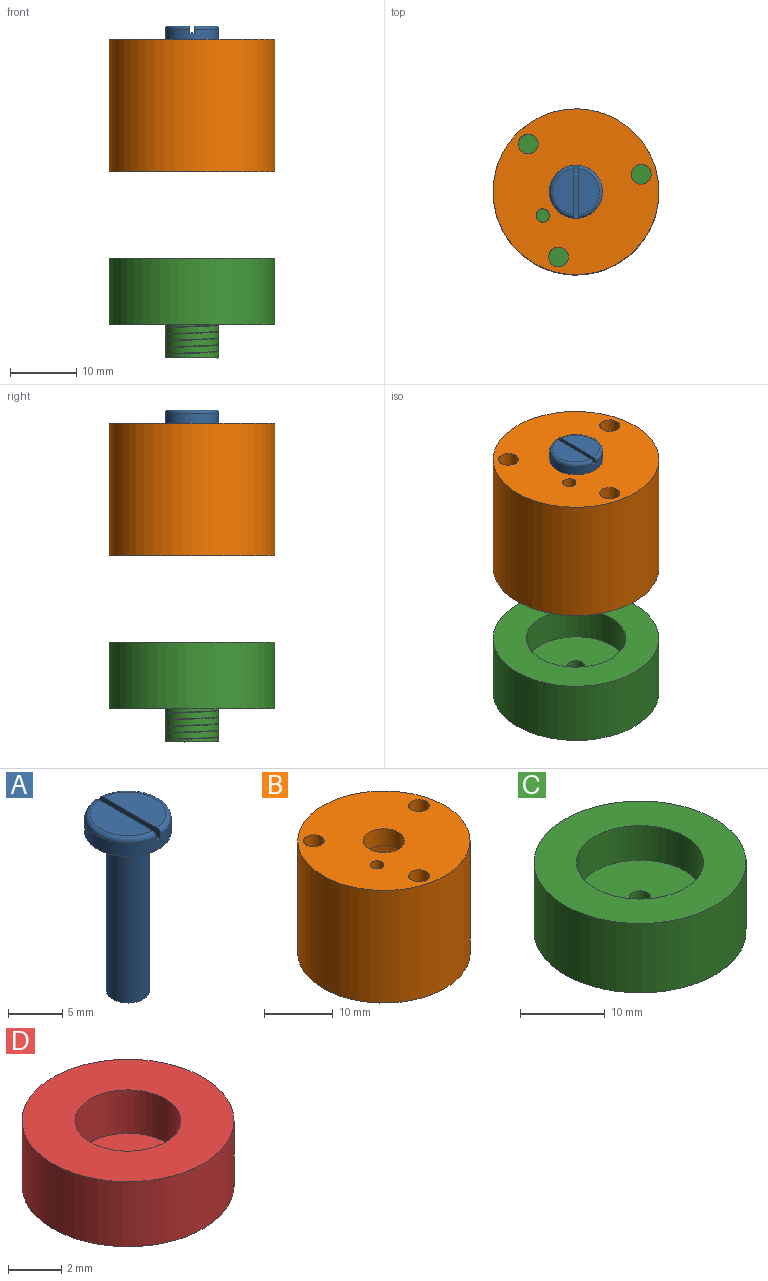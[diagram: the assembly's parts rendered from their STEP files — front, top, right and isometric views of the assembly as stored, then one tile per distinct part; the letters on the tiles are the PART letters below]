
ASSEMBLY  parts=4 mates=4
PART A: 11 faces, bbox 8.7x8.7x20 mm
  f0: plane 6.97x3.19mm, normal (0,0,1), area 17.1mm2, adj f7,f9
  f1: torus R=3.5mm, axis (0,0,-1), area 8.9mm2, adj f5,f6,f10
  f2: plane 8x8mm, normal (0,0,-1), area 37.7mm2, adj f3,f6
  f3: cylinder r=2mm len=18mm, axis (0,0,1), area 226.2mm2, adj f2,f4
  f4: plane 4x4mm, normal (0,0,-1), area 12.6mm2, adj f3
  f5: plane 6.97x3.2mm, normal (0,0,1), area 17.1mm2, adj f1,f10
  f6: cylinder r=4mm len=8mm, axis (0,0,1), area 37.1mm2, adj f1,f2,f7,f8,f9,f10
  f7: torus R=3.5mm, axis (0,0,-1), area 8.9mm2, adj f0,f6,f9
  f8: plane 8x0.61mm, normal (0,0,1), area 4.9mm2, adj f6,f9,f10
  f9: plane 7.98x1mm, normal (1,0,0), area 7.9mm2, adj f0,f6,f7,f8
  f10: plane 8x1.02mm, normal (-1,0,0), area 7.9mm2, adj f1,f5,f6,f8
PART B: 10 faces, bbox 25x25x20 mm
  f0: plane 25x25mm, normal (0,0,1), area 438.3mm2, adj f4,f5,f6,f7,f8,f9
  f1: plane 15x15mm, normal (0,0,-1), area 145.3mm2, adj f2,f5,f9
  f2: cylinder r=7.5mm len=17mm, axis (0,0,-1), area 801.1mm2, adj f1,f3
  f3: plane 25x25mm, normal (0,0,-1), area 293mm2, adj f2,f4,f6,f7,f8
  f4: cylinder r=12.5mm len=25mm, axis (0,0,-1), area 1570.8mm2, adj f0,f3
  f5: cylinder r=3mm len=6mm, axis (0,0,1), area 56.5mm2, adj f0,f1
  f6: cylinder r=1.5mm len=20mm, axis (0,0,1), area 188.5mm2, adj f0,f3
  f7: cylinder r=1.5mm len=20mm, axis (0,0,1), area 188.5mm2, adj f0,f3
  f8: cylinder r=1.5mm len=20mm, axis (0,0,1), area 188.5mm2, adj f0,f3
  f9: cylinder r=1mm len=3mm, axis (0,0,1), area 18.8mm2, adj f0,f1
PART C: 14 faces, bbox 25x25x15.1 mm
  f0: cylinder r=4mm len=0.03mm, axis (0,0,1), area 0mm2, adj f2
  f1: cylinder r=4mm len=8mm, axis (0,0,1), area 144.8mm2, adj f2,f3,f8,f9,f11,f12
  f2: plane 8.01x8.01mm, normal (0,0,-1), area 45.4mm2, adj f0,f1,f8,f9,f13
  f3: plane 25.01x25.01mm, normal (0,0,-1), area 440.6mm2, adj f1,f4,f10,f12
  f4: cylinder r=12.5mm len=25mm, axis (0,0,1), area 785.4mm2, adj f3,f5
  f5: plane 25x25mm, normal (0,0,1), area 314.2mm2, adj f4,f6
  f6: cylinder r=7.5mm len=15mm, axis (0,0,1), area 235.6mm2, adj f5,f7
  f7: plane 15x15mm, normal (0,0,1), area 171.8mm2, adj f6,f13
  f8: bspline ~7.99x7.99mm, area 8.8mm2, adj f1,f2,f9,f11,f12
  f9: plane 0.06x0.05mm, normal (0,1,0), area 0mm2, adj f1,f2,f8,f12
  f10: cylinder r=4mm len=1.31mm, axis (0,0,1), area 0mm2, adj f3,f11,f12
  f11: plane 0.1x0.05mm, normal (0,-1,0), area 0mm2, adj f1,f8,f10,f12
  f12: bspline ~9.24x8mm, area 9.5mm2, adj f1,f3,f8,f9,f10,f11
  f13: cylinder r=1.25mm len=10mm, axis (0,0,1), area 78.5mm2, adj f2,f7
PART D: 5 faces, bbox 8x8x3 mm
  f0: plane 8x8mm, normal (0,0,1), area 37.7mm2, adj f1,f4
  f1: cylinder r=2mm len=4mm, axis (0,0,-1), area 25.1mm2, adj f0,f2
  f2: plane 4x4mm, normal (0,0,1), area 12.6mm2, adj f1
  f3: plane 8x8mm, normal (0,0,-1), area 50.3mm2, adj f4
  f4: cylinder r=4mm len=8mm, axis (0,0,-1), area 75.4mm2, adj f0,f3
PLACE A rot(axis=(-0.02,-0.15,0.99),0deg) t=(-72.63,-145.42,-40.58)mm
PLACE B rot(axis=(-0.01,-0.14,0.99),0deg) t=(-72.63,-104.33,-85.14)mm
PLACE C rot(axis=(-0.01,-0.14,0.99),0deg) t=(-72.63,-104.33,-55.63)mm
PLACE D rot(axis=(-0.01,-0.14,0.99),0deg) t=(-72.63,-78.36,-55.62)mm
MATE slider C.f0 <-> D.f1  axis (0,0,1) through (-72.63,-104.33,-69.66)mm
MATE cylindrical B.f2 <-> C.f0  axis (0,0,-1) through (-72.63,-104.33,-56.62)mm
MATE fastened B.f2 <-> D.f1  axis (0,0,-1) through (-72.63,-104.33,-56.62)mm
MATE revolute D.f1 <-> A.f1  axis (0,0,-1) through (-72.63,-104.33,-54.62)mm
